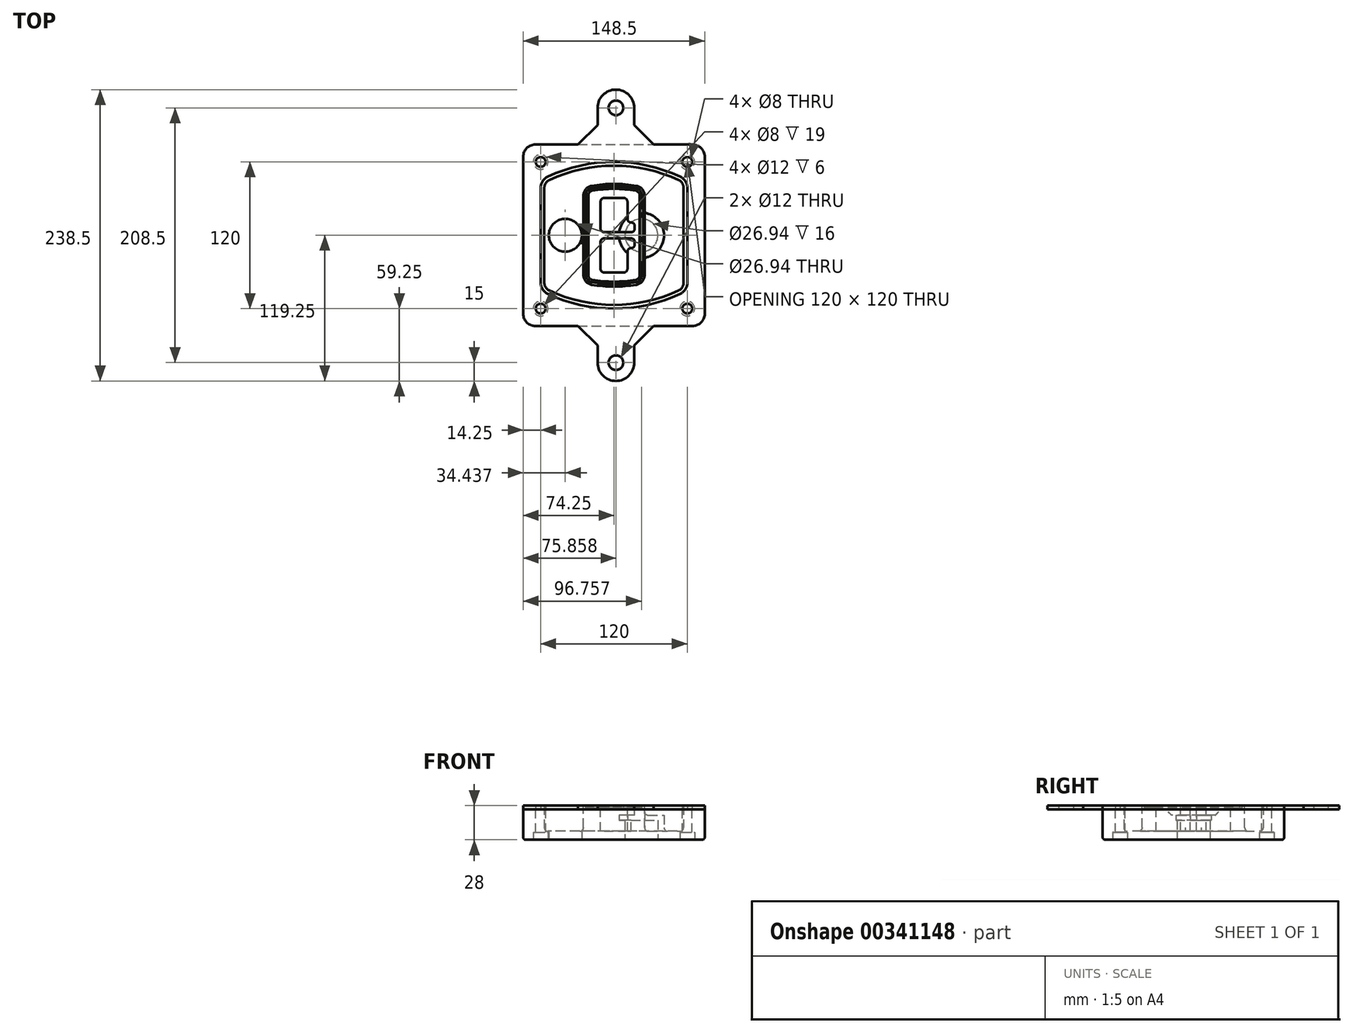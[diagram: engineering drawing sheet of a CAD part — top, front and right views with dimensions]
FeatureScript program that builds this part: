
annotation { "Feature Type Name" : "Feature", "Feature Type Description" : "" }
export const myFeature = defineFeature(function(context is Context, id is Id, definition is map)
    precondition{}
    {
        {
            var Q0;
            Q0=qCreatedBy(makeId("Top.planeOp"),FACE);
            var sketch = newSketch(context, id + "F0", { "sketchPlane" : qUnion([Q0])});
            skPoint(sketch, "E0.rect.middle", {"position": v(0, 0) * mm});
            skLineSegment(sketch, "E1.bottom", {"start": v(-64.25, -74.25) * mm, "end": v(64.25, -74.25) * mm});
            skLineSegment(sketch, "E1.top", {"start": v(-64.25, 74.25) * mm, "end": v(64.25, 74.25) * mm});
            skLineSegment(sketch, "E1.left", {"start": v(-74.25, -64.25) * mm, "end": v(-74.25, 64.25) * mm});
            skLineSegment(sketch, "E1.right", {"start": v(74.25, -64.25) * mm, "end": v(74.25, 64.25) * mm});
            skLineSegment(sketch, "E2", {"start": v(-74.25, 74.25) * mm, "end": v(74.25, -74.25) * mm, "construction": true});
            skLineSegment(sketch, "E3", {"start": v(74.25, 74.25) * mm, "end": v(-74.25, -74.25) * mm, "construction": true});
            skCircle(sketch, "E4", {"center": v(-60, 60) * mm, "radius": 4 * mm});
            skCircle(sketch, "E5", {"center": v(60, 60) * mm, "radius": 4 * mm});
            skCircle(sketch, "E6", {"center": v(60, -60) * mm, "radius": 4 * mm});
            skCircle(sketch, "E7", {"center": v(-60, -60) * mm, "radius": 4 * mm});
            skLineSegment(sketch, "E8", {"start": v(-60, 60) * mm, "end": v(60, 60) * mm, "construction": true});
            skLineSegment(sketch, "E9", {"start": v(60, 60) * mm, "end": v(60, -60) * mm, "construction": true});
            skLineSegment(sketch, "E10", {"start": v(60, -60) * mm, "end": v(-60, -60) * mm, "construction": true});
            skLineSegment(sketch, "E11", {"start": v(-60, -60) * mm, "end": v(-60, 60) * mm, "construction": true});
            skLineSegment(sketch, "E12", {"start": v(-60, 38.83) * mm, "end": v(-60, -38.83) * mm});
            skLineSegment(sketch, "E13", {"start": v(60, 38.83) * mm, "end": v(60, -38.83) * mm});
            skArc(sketch, "E14", {"start": v(54.26, 47.88) * mm, "mid": v(0, 60) * mm, "end": v(-54.26, 47.88) * mm});
            skArc(sketch, "E15", {"start": v(-54.26, -47.88) * mm, "mid": v(0, -60) * mm, "end": v(54.26, -47.88) * mm});
            skLineSegment(sketch, "E16", {"start": v(-60, 0) * mm, "end": v(60, 0) * mm, "construction": true});
            skPoint(sketch, "E17.visualSharp", {"position": v(-60, -45) * mm});
            skArc(sketch, "E17.filletArc", {"start": v(-60, -38.83) * mm, "mid": v(-58.44, -44.2) * mm, "end": v(-54.26, -47.88) * mm});
            skPoint(sketch, "E18.visualSharp", {"position": v(-60, 45) * mm});
            skArc(sketch, "E18.filletArc", {"start": v(-54.26, 47.88) * mm, "mid": v(-58.44, 44.2) * mm, "end": v(-60, 38.83) * mm});
            skPoint(sketch, "E19.visualSharp", {"position": v(60, 45) * mm});
            skArc(sketch, "E19.filletArc", {"start": v(60, 38.83) * mm, "mid": v(58.44, 44.2) * mm, "end": v(54.26, 47.88) * mm});
            skPoint(sketch, "E20.visualSharp", {"position": v(60, -45) * mm});
            skArc(sketch, "E20.filletArc", {"start": v(54.26, -47.88) * mm, "mid": v(58.44, -44.2) * mm, "end": v(60, -38.83) * mm});
            skPoint(sketch, "E21.visualSharp", {"position": v(-74.25, 74.25) * mm});
            skArc(sketch, "E21.filletArc", {"start": v(-64.25, 74.25) * mm, "mid": v(-71.32, 71.32) * mm, "end": v(-74.25, 64.25) * mm});
            skPoint(sketch, "E22.visualSharp", {"position": v(74.25, 74.25) * mm});
            skArc(sketch, "E22.filletArc", {"start": v(74.25, 64.25) * mm, "mid": v(71.32, 71.32) * mm, "end": v(64.25, 74.25) * mm});
            skPoint(sketch, "E23.visualSharp", {"position": v(74.25, -74.25) * mm});
            skArc(sketch, "E23.filletArc", {"start": v(64.25, -74.25) * mm, "mid": v(71.32, -71.32) * mm, "end": v(74.25, -64.25) * mm});
            skPoint(sketch, "E24.visualSharp", {"position": v(-74.25, -74.25) * mm});
            skArc(sketch, "E24.filletArc", {"start": v(-74.25, -64.25) * mm, "mid": v(-71.32, -71.32) * mm, "end": v(-64.25, -74.25) * mm});
            skArc(sketch, "E25.0", {"start": v(57, 38.83) * mm, "mid": v(55.9, 42.58) * mm, "end": v(52.98, 45.17) * mm});
            skLineSegment(sketch, "E25.1", {"start": v(57, 38.83) * mm, "end": v(57, -38.83) * mm});
            skArc(sketch, "E25.2", {"start": v(52.98, -45.17) * mm, "mid": v(55.9, -42.58) * mm, "end": v(57, -38.83) * mm});
            skArc(sketch, "E25.3", {"start": v(-52.98, -45.17) * mm, "mid": v(0, -57) * mm, "end": v(52.98, -45.17) * mm});
            skArc(sketch, "E25.4", {"start": v(-57, -38.83) * mm, "mid": v(-55.9, -42.58) * mm, "end": v(-52.98, -45.17) * mm});
            skArc(sketch, "E25.5", {"start": v(52.98, 45.17) * mm, "mid": v(0, 57) * mm, "end": v(-52.98, 45.17) * mm});
            skLineSegment(sketch, "E25.6", {"start": v(-57, 38.83) * mm, "end": v(-57, -38.83) * mm});
            skArc(sketch, "E25.7", {"start": v(-52.98, 45.17) * mm, "mid": v(-55.9, 42.58) * mm, "end": v(-57, 38.83) * mm});
            skArc(sketch, "E26.0", {"start": v(-55.96, 51.5) * mm, "mid": v(-61.82, 46.33) * mm, "end": v(-64, 38.83) * mm});
            skArc(sketch, "E26.1", {"start": v(55.96, 51.5) * mm, "mid": v(0, 64) * mm, "end": v(-55.96, 51.5) * mm});
            skArc(sketch, "E26.2", {"start": v(64, 38.83) * mm, "mid": v(61.82, 46.33) * mm, "end": v(55.96, 51.5) * mm});
            skLineSegment(sketch, "E26.3", {"start": v(64, 38.83) * mm, "end": v(64, -38.83) * mm});
            skArc(sketch, "E26.4", {"start": v(55.96, -51.5) * mm, "mid": v(61.82, -46.33) * mm, "end": v(64, -38.83) * mm});
            skLineSegment(sketch, "E26.5", {"start": v(-64, 38.83) * mm, "end": v(-64, -38.83) * mm});
            skArc(sketch, "E26.6", {"start": v(-55.96, -51.5) * mm, "mid": v(0, -64) * mm, "end": v(55.96, -51.5) * mm});
            skArc(sketch, "E26.7", {"start": v(-64, -38.83) * mm, "mid": v(-61.82, -46.33) * mm, "end": v(-55.96, -51.5) * mm});
            skSolve(sketch);
        }
        {
            var Q0;
            Q0=makeQuery(id+"F0.imprint","IMPRINT",FACE,{"disambiguationData":[TD([[makeQuery(id+"F0.imprint","IMPRINT",EDGE,{"derivedFrom":sQuery(id+"F0.wireOp",EDGE,"E1.bottom")}),1.0]])]});
            var Q1;
            Q1=makeQuery(id+"F0.imprint","IMPRINT",FACE,{"disambiguationData":[TD([[makeQuery(id+"F0.imprint","IMPRINT",EDGE,{"derivedFrom":sQuery(id+"F0.wireOp",EDGE,"E12")}),1.0]])]});
            var Q2;
            Q2=makeQuery(id+"F0.imprint","IMPRINT",FACE,{"disambiguationData":[TD([[makeQuery(id+"F0.imprint","IMPRINT",EDGE,{"derivedFrom":sQuery(id+"F0.wireOp",EDGE,"E25.0")}),1.0]])]});
            var Q3;
            Q3=makeQuery(id+"F0.imprint","IMPRINT",FACE,{"disambiguationData":[TD([[makeQuery(id+"F0.imprint","IMPRINT",EDGE,{"derivedFrom":sQuery(id+"F0.wireOp",EDGE,"E12")}),-1.0]])]});
            extrude(context, id + "F1", {"entities" : qUnion([Q0, Q1, Q2, Q3]), "oppositeDirection" : true, "depth" : 25 * mm});
        }
        {
            var Q0;
            Q0=makeQuery(id+"F0.imprint","IMPRINT",FACE,{"disambiguationData":[TD([[makeQuery(id+"F0.imprint","IMPRINT",EDGE,{"derivedFrom":sQuery(id+"F0.wireOp",EDGE,"E12")}),1.0]])]});
            extrude(context, id + "F2", {"entities" : qUnion([Q0]), "operationType" : NewBodyOperationType.ADD, "depth" : 3 * mm});
        }
        {
            var Q0;
            Q0=makeQuery(id+"F0.imprint","IMPRINT",FACE,{"disambiguationData":[TD([[makeQuery(id+"F0.imprint","IMPRINT",EDGE,{"derivedFrom":sQuery(id+"F0.wireOp",EDGE,"E25.0")}),1.0]])]});
            extrude(context, id + "F3", {"entities" : qUnion([Q0]), "operationType" : NewBodyOperationType.REMOVE, "oppositeDirection" : true, "depth" : 18 * mm});
        }
        {
            var Q0;
            Q0=makeQuery(id+"F2.opExtrude","CAP_FACE",FACE,{"disambiguationData":[OSD([sQuery(id+"F0.wireOp",EDGE,"E12"),sQuery(id+"F0.wireOp",EDGE,"E13"),sQuery(id+"F0.wireOp",EDGE,"E14"),sQuery(id+"F0.wireOp",EDGE,"E15"),sQuery(id+"F0.wireOp",EDGE,"E17.filletArc"),sQuery(id+"F0.wireOp",EDGE,"E18.filletArc"),sQuery(id+"F0.wireOp",EDGE,"E19.filletArc"),sQuery(id+"F0.wireOp",EDGE,"E20.filletArc"),sQuery(id+"F0.wireOp",EDGE,"E25.0"),sQuery(id+"F0.wireOp",EDGE,"E25.1"),sQuery(id+"F0.wireOp",EDGE,"E25.2"),sQuery(id+"F0.wireOp",EDGE,"E25.3"),sQuery(id+"F0.wireOp",EDGE,"E25.4"),sQuery(id+"F0.wireOp",EDGE,"E25.5"),sQuery(id+"F0.wireOp",EDGE,"E25.6"),sQuery(id+"F0.wireOp",EDGE,"E25.7")])],"isStart":false});
            var sketch = newSketch(context, id + "F4", { "sketchPlane" : qUnion([Q0])});
            skArc(sketch, "E27.0", {"start": v(-18.34, -40.45) * mm, "mid": v(0, -42) * mm, "end": v(18.34, -40.45) * mm});
            skArc(sketch, "E28.0", {"start": v(18.34, 40.45) * mm, "mid": v(0, 42) * mm, "end": v(-18.34, 40.45) * mm});
            skLineSegment(sketch, "E29", {"start": v(-25, 32.57) * mm, "end": v(-25, -32.57) * mm});
            skLineSegment(sketch, "E30", {"start": v(25, 32.57) * mm, "end": v(25, -32.57) * mm});
            skLineSegment(sketch, "E31", {"start": v(-25, 39.1) * mm, "end": v(25, 39.1) * mm, "construction": true});
            skLineSegment(sketch, "E32", {"start": v(-25, -39.1) * mm, "end": v(25, -39.1) * mm, "construction": true});
            skPoint(sketch, "E33.visualSharp", {"position": v(-25, 39.1) * mm});
            skArc(sketch, "E33.filletArc", {"start": v(-18.34, 40.45) * mm, "mid": v(-23.11, 37.73) * mm, "end": v(-25, 32.57) * mm});
            skPoint(sketch, "E34.visualSharp", {"position": v(25, 39.1) * mm});
            skArc(sketch, "E34.filletArc", {"start": v(25, 32.57) * mm, "mid": v(23.11, 37.73) * mm, "end": v(18.34, 40.45) * mm});
            skPoint(sketch, "E35.visualSharp", {"position": v(25, -39.1) * mm});
            skArc(sketch, "E35.filletArc", {"start": v(18.34, -40.45) * mm, "mid": v(23.11, -37.73) * mm, "end": v(25, -32.57) * mm});
            skPoint(sketch, "E36.visualSharp", {"position": v(-25, -39.1) * mm});
            skArc(sketch, "E36.filletArc", {"start": v(-25, -32.57) * mm, "mid": v(-23.11, -37.73) * mm, "end": v(-18.34, -40.45) * mm});
            skArc(sketch, "E37.0", {"start": v(52.98, 45.17) * mm, "mid": v(0, 57) * mm, "end": v(-52.98, 45.17) * mm});
            skArc(sketch, "E37.1", {"start": v(-52.98, 45.17) * mm, "mid": v(-55.9, 42.58) * mm, "end": v(-57, 38.83) * mm});
            skLineSegment(sketch, "E37.2", {"start": v(-57, 38.83) * mm, "end": v(-57, -38.83) * mm});
            skArc(sketch, "E37.3", {"start": v(-57, -38.83) * mm, "mid": v(-55.9, -42.58) * mm, "end": v(-52.98, -45.17) * mm});
            skArc(sketch, "E37.4", {"start": v(-52.98, -45.17) * mm, "mid": v(0, -57) * mm, "end": v(52.98, -45.17) * mm});
            skArc(sketch, "E37.5", {"start": v(52.98, -45.17) * mm, "mid": v(55.9, -42.58) * mm, "end": v(57, -38.83) * mm});
            skLineSegment(sketch, "E37.6", {"start": v(57, 38.83) * mm, "end": v(57, -38.83) * mm});
            skArc(sketch, "E37.7", {"start": v(57, 38.83) * mm, "mid": v(55.9, 42.58) * mm, "end": v(52.98, 45.17) * mm});
            skLineSegment(sketch, "E38.0", {"start": v(23, 32.57) * mm, "end": v(23, -32.57) * mm});
            skArc(sketch, "E38.1", {"start": v(18, -38.48) * mm, "mid": v(21.58, -36.44) * mm, "end": v(23, -32.57) * mm});
            skArc(sketch, "E38.2", {"start": v(-18, -38.48) * mm, "mid": v(0, -40) * mm, "end": v(18, -38.48) * mm});
            skArc(sketch, "E38.3", {"start": v(-23, -32.57) * mm, "mid": v(-21.58, -36.44) * mm, "end": v(-18, -38.48) * mm});
            skLineSegment(sketch, "E38.4", {"start": v(-23, 32.57) * mm, "end": v(-23, -32.57) * mm});
            skArc(sketch, "E38.5", {"start": v(23, 32.57) * mm, "mid": v(21.58, 36.44) * mm, "end": v(18, 38.48) * mm});
            skArc(sketch, "E38.6", {"start": v(-18, 38.48) * mm, "mid": v(-21.58, 36.44) * mm, "end": v(-23, 32.57) * mm});
            skArc(sketch, "E38.7", {"start": v(18, 38.48) * mm, "mid": v(0, 40) * mm, "end": v(-18, 38.48) * mm});
            skArc(sketch, "E39.0", {"start": v(21, 32.57) * mm, "mid": v(20.06, 35.15) * mm, "end": v(17.67, 36.5) * mm});
            skLineSegment(sketch, "E39.1", {"start": v(21, 32.57) * mm, "end": v(21, -32.57) * mm});
            skArc(sketch, "E39.2", {"start": v(17.67, -36.5) * mm, "mid": v(20.06, -35.15) * mm, "end": v(21, -32.57) * mm});
            skArc(sketch, "E39.3", {"start": v(-17.67, -36.5) * mm, "mid": v(0, -38) * mm, "end": v(17.67, -36.5) * mm});
            skArc(sketch, "E39.4", {"start": v(-21, -32.57) * mm, "mid": v(-20.06, -35.15) * mm, "end": v(-17.67, -36.5) * mm});
            skArc(sketch, "E39.5", {"start": v(17.67, 36.5) * mm, "mid": v(0, 38) * mm, "end": v(-17.67, 36.5) * mm});
            skLineSegment(sketch, "E39.6", {"start": v(-21, 32.57) * mm, "end": v(-21, -32.57) * mm});
            skArc(sketch, "E39.7", {"start": v(-17.67, 36.5) * mm, "mid": v(-20.06, 35.15) * mm, "end": v(-21, 32.57) * mm});
            skLineSegment(sketch, "E40", {"start": v(-25, 0) * mm, "end": v(25, 0) * mm, "construction": true});
            skLineSegment(sketch, "E41", {"start": v(-11, 5.5) * mm, "end": v(-11, 27.5) * mm});
            skLineSegment(sketch, "E42", {"start": v(-8, 30.5) * mm, "end": v(8, 30.5) * mm});
            skLineSegment(sketch, "E43", {"start": v(11, 27.5) * mm, "end": v(11, 13.5) * mm});
            skLineSegment(sketch, "E44", {"start": v(14, 10.5) * mm, "end": v(14, 10.5) * mm});
            skLineSegment(sketch, "E45", {"start": v(17, 7.5) * mm, "end": v(17, 5.5) * mm});
            skLineSegment(sketch, "E46", {"start": v(14, 2.5) * mm, "end": v(-8, 2.5) * mm});
            skPoint(sketch, "E47.visualSharp", {"position": v(-11, 30.5) * mm});
            skArc(sketch, "E47.filletArc", {"start": v(-8, 30.5) * mm, "mid": v(-10.12, 29.62) * mm, "end": v(-11, 27.5) * mm});
            skPoint(sketch, "E48.visualSharp", {"position": v(11, 30.5) * mm});
            skArc(sketch, "E48.filletArc", {"start": v(11, 27.5) * mm, "mid": v(10.12, 29.62) * mm, "end": v(8, 30.5) * mm});
            skPoint(sketch, "E49.visualSharp", {"position": v(11, 10.5) * mm});
            skArc(sketch, "E49.filletArc", {"start": v(11, 13.5) * mm, "mid": v(11.88, 11.38) * mm, "end": v(14, 10.5) * mm});
            skPoint(sketch, "E50.visualSharp", {"position": v(17, 10.5) * mm});
            skArc(sketch, "E50.filletArc", {"start": v(17, 7.5) * mm, "mid": v(16.12, 9.62) * mm, "end": v(14, 10.5) * mm});
            skPoint(sketch, "E51.visualSharp", {"position": v(17, 2.5) * mm});
            skArc(sketch, "E51.filletArc", {"start": v(14, 2.5) * mm, "mid": v(16.12, 3.38) * mm, "end": v(17, 5.5) * mm});
            skPoint(sketch, "E52.visualSharp", {"position": v(-11, 2.5) * mm});
            skArc(sketch, "E52.filletArc", {"start": v(-11, 5.5) * mm, "mid": v(-10.12, 3.38) * mm, "end": v(-8, 2.5) * mm});
            skLineSegment(sketch, "E53.0.MirrorCS", {"start": v(14, -2.5) * mm, "end": v(-8, -2.5) * mm});
            skArc(sketch, "E54.0.MirrorCS", {"start": v(-11, -5.5) * mm, "mid": v(-10.12, -3.38) * mm, "end": v(-8, -2.5) * mm});
            skLineSegment(sketch, "E55.0.MirrorCS", {"start": v(-11, -5.5) * mm, "end": v(-11, -27.5) * mm});
            skArc(sketch, "E56.0.MirrorCS", {"start": v(-8, -30.5) * mm, "mid": v(-10.12, -29.62) * mm, "end": v(-11, -27.5) * mm});
            skLineSegment(sketch, "E57.0.MirrorCS", {"start": v(-8, -30.5) * mm, "end": v(8, -30.5) * mm});
            skArc(sketch, "E58.0.MirrorCS", {"start": v(11, -27.5) * mm, "mid": v(10.12, -29.62) * mm, "end": v(8, -30.5) * mm});
            skLineSegment(sketch, "E59.0.MirrorCS", {"start": v(11, -27.5) * mm, "end": v(11, -13.5) * mm});
            skArc(sketch, "E60.0.MirrorCS", {"start": v(11, -13.5) * mm, "mid": v(11.88, -11.38) * mm, "end": v(14, -10.5) * mm});
            skArc(sketch, "E61.0.MirrorCS", {"start": v(17, -7.5) * mm, "mid": v(16.12, -9.62) * mm, "end": v(14, -10.5) * mm});
            skLineSegment(sketch, "E62.0.MirrorCS", {"start": v(17, -7.5) * mm, "end": v(17, -5.5) * mm});
            skArc(sketch, "E63.0.MirrorCS", {"start": v(14, -2.5) * mm, "mid": v(16.12, -3.38) * mm, "end": v(17, -5.5) * mm});
            skSolve(sketch);
        }
        {
            var Q0;
            Q0=makeQuery(id+"F4.imprint","IMPRINT",FACE,{"disambiguationData":[TD([[makeQuery(id+"F4.imprint","IMPRINT",EDGE,{"derivedFrom":sQuery(id+"F4.wireOp",EDGE,"E27.0")}),1.0]])]});
            var Q1;
            Q1=makeQuery(id+"F4.imprint","IMPRINT",FACE,{"disambiguationData":[TD([[makeQuery(id+"F4.imprint","IMPRINT",EDGE,{"derivedFrom":sQuery(id+"F4.wireOp",EDGE,"E38.0")}),-1.0]])]});
            var Q2;
            Q2=makeQuery(id+"F4.imprint","IMPRINT",FACE,{"disambiguationData":[TD([[makeQuery(id+"F4.imprint","IMPRINT",EDGE,{"derivedFrom":sQuery(id+"F4.wireOp",EDGE,"E39.0")}),1.0]])]});
            extrude(context, id + "F5", {"entities" : qUnion([Q0, Q1, Q2]), "operationType" : NewBodyOperationType.ADD, "endBound" : BoundingType.UP_TO_NEXT, "oppositeDirection" : true, "depth" : 25 * mm});
        }
        {
            var Q0;
            Q0=makeQuery(id+"F4.imprint","IMPRINT",FACE,{"disambiguationData":[TD([[makeQuery(id+"F4.imprint","IMPRINT",EDGE,{"derivedFrom":sQuery(id+"F4.wireOp",EDGE,"E38.0")}),-1.0]])]});
            extrude(context, id + "F6", {"entities" : qUnion([Q0]), "operationType" : NewBodyOperationType.REMOVE, "oppositeDirection" : true, "depth" : 2 * mm});
        }
        {
            var Q0;
            Q0=makeQuery(id+"F1.opExtrude","CAP_FACE",FACE,{"disambiguationData":[OSD([sQuery(id+"F0.wireOp",EDGE,"E1.bottom"),sQuery(id+"F0.wireOp",EDGE,"E1.top"),sQuery(id+"F0.wireOp",EDGE,"E1.left"),sQuery(id+"F0.wireOp",EDGE,"E1.right"),sQuery(id+"F0.wireOp",EDGE,"E4"),sQuery(id+"F0.wireOp",EDGE,"E5"),sQuery(id+"F0.wireOp",EDGE,"E6"),sQuery(id+"F0.wireOp",EDGE,"E7"),sQuery(id+"F0.wireOp",EDGE,"E21.filletArc"),sQuery(id+"F0.wireOp",EDGE,"E22.filletArc"),sQuery(id+"F0.wireOp",EDGE,"E23.filletArc"),sQuery(id+"F0.wireOp",EDGE,"E24.filletArc")])],"isStart":false});
            var sketch = newSketch(context, id + "F7", { "sketchPlane" : qUnion([Q0])});
            skCircle(sketch, "E64", {"center": v(22.5, 0) * mm, "radius": 13.47 * mm});
            skCircle(sketch, "E65", {"center": v(-39.81, 0) * mm, "radius": 13.47 * mm});
            skLineSegment(sketch, "E66", {"start": v(74.25, 0) * mm, "end": v(-74.25, 0) * mm});
            skCircle(sketch, "E67", {"center": v(22.5, 0) * mm, "radius": 18.47 * mm});
            skCircle(sketch, "E68", {"center": v(60, -60) * mm, "radius": 6 * mm});
            skCircle(sketch, "E69", {"center": v(-60, -60) * mm, "radius": 6 * mm});
            skCircle(sketch, "E70", {"center": v(-60, 60) * mm, "radius": 6 * mm});
            skCircle(sketch, "E71", {"center": v(60, 60) * mm, "radius": 6 * mm});
            skSolve(sketch);
        }
        {
            var Q0;
            {var subQ1=sQuery(id+"F7.wireOp",EDGE,"E66");var subQ4=sQuery(id+"F7.wireOp",EDGE,"E64");var subQ6=makeQuery(id+"F7.imprint","INTERSECT",VERTEX,{"disambiguationData":[OD(0.0)],"derivedFrom":[subQ4,subQ1]});Q0=makeQuery(id+"F7.imprint","IMPRINT",FACE,{"disambiguationData":[TD([[makeQuery(id+"F7.imprint","IMPRINT",EDGE,{"disambiguationData":[TD([[subQ6,-1.0]])],"derivedFrom":subQ4}),-1.0]])]});}
            var Q1;
            {var subQ0=sQuery(id+"F7.wireOp",EDGE,"E66");var subQ1=sQuery(id+"F7.wireOp",EDGE,"E64");var subQ3=makeQuery(id+"F7.imprint","INTERSECT",VERTEX,{"disambiguationData":[OD(0.0)],"derivedFrom":[subQ1,subQ0]});Q1=makeQuery(id+"F7.imprint","IMPRINT",FACE,{"disambiguationData":[TD([[makeQuery(id+"F7.imprint","IMPRINT",EDGE,{"disambiguationData":[TD([[subQ3,-1.0]])],"derivedFrom":subQ1}),1.0]])]});}
            var Q2;
            {var subQ0=sQuery(id+"F7.wireOp",EDGE,"E66");var subQ1=sQuery(id+"F7.wireOp",EDGE,"E64");var subQ3=makeQuery(id+"F7.imprint","INTERSECT",VERTEX,{"disambiguationData":[OD(0.0)],"derivedFrom":[subQ1,subQ0]});Q2=makeQuery(id+"F7.imprint","IMPRINT",FACE,{"disambiguationData":[TD([[makeQuery(id+"F7.imprint","IMPRINT",EDGE,{"disambiguationData":[TD([[subQ3,1.0]])],"derivedFrom":subQ1}),1.0]])]});}
            var Q3;
            {var subQ1=sQuery(id+"F7.wireOp",EDGE,"E66");var subQ4=sQuery(id+"F7.wireOp",EDGE,"E64");var subQ6=makeQuery(id+"F7.imprint","INTERSECT",VERTEX,{"disambiguationData":[OD(0.0)],"derivedFrom":[subQ4,subQ1]});Q3=makeQuery(id+"F7.imprint","IMPRINT",FACE,{"disambiguationData":[TD([[makeQuery(id+"F7.imprint","IMPRINT",EDGE,{"disambiguationData":[TD([[subQ6,1.0]])],"derivedFrom":subQ4}),-1.0]])]});}
            extrude(context, id + "F8", {"entities" : qUnion([Q0, Q1, Q2, Q3]), "operationType" : NewBodyOperationType.ADD, "oppositeDirection" : true, "depth" : 20 * mm});
        }
        {
            var Q0;
            {var subQ0=sQuery(id+"F7.wireOp",EDGE,"E66");var subQ1=sQuery(id+"F7.wireOp",EDGE,"E64");var subQ3=makeQuery(id+"F7.imprint","INTERSECT",VERTEX,{"disambiguationData":[OD(0.0)],"derivedFrom":[subQ1,subQ0]});Q0=makeQuery(id+"F7.imprint","IMPRINT",FACE,{"disambiguationData":[TD([[makeQuery(id+"F7.imprint","IMPRINT",EDGE,{"disambiguationData":[TD([[subQ3,-1.0]])],"derivedFrom":subQ1}),1.0]])]});}
            var Q1;
            {var subQ0=sQuery(id+"F7.wireOp",EDGE,"E66");var subQ1=sQuery(id+"F7.wireOp",EDGE,"E64");var subQ3=makeQuery(id+"F7.imprint","INTERSECT",VERTEX,{"disambiguationData":[OD(0.0)],"derivedFrom":[subQ1,subQ0]});Q1=makeQuery(id+"F7.imprint","IMPRINT",FACE,{"disambiguationData":[TD([[makeQuery(id+"F7.imprint","IMPRINT",EDGE,{"disambiguationData":[TD([[subQ3,1.0]])],"derivedFrom":subQ1}),1.0]])]});}
            extrude(context, id + "F9", {"entities" : qUnion([Q0, Q1]), "operationType" : NewBodyOperationType.REMOVE, "oppositeDirection" : true, "depth" : 16 * mm});
        }
        {
            var Q0;
            {var subQ0=sQuery(id+"F7.wireOp",EDGE,"E66");var subQ1=sQuery(id+"F7.wireOp",EDGE,"E65");var subQ3=makeQuery(id+"F7.imprint","INTERSECT",VERTEX,{"disambiguationData":[OD(0.0)],"derivedFrom":[subQ1,subQ0]});Q0=makeQuery(id+"F7.imprint","IMPRINT",FACE,{"disambiguationData":[TD([[makeQuery(id+"F7.imprint","IMPRINT",EDGE,{"disambiguationData":[TD([[subQ3,-1.0]])],"derivedFrom":subQ1}),1.0]])]});}
            var Q1;
            {var subQ0=sQuery(id+"F7.wireOp",EDGE,"E66");var subQ1=sQuery(id+"F7.wireOp",EDGE,"E65");var subQ3=makeQuery(id+"F7.imprint","INTERSECT",VERTEX,{"disambiguationData":[OD(0.0)],"derivedFrom":[subQ1,subQ0]});Q1=makeQuery(id+"F7.imprint","IMPRINT",FACE,{"disambiguationData":[TD([[makeQuery(id+"F7.imprint","IMPRINT",EDGE,{"disambiguationData":[TD([[subQ3,1.0]])],"derivedFrom":subQ1}),1.0]])]});}
            extrude(context, id + "F10", {"entities" : qUnion([Q0, Q1]), "operationType" : NewBodyOperationType.REMOVE, "oppositeDirection" : true, "depth" : 25 * mm});
        }
        {
            var Q0;
            Q0=makeQuery(id+"F7.imprint","IMPRINT",FACE,{"disambiguationData":[TD([[makeQuery(id+"F7.imprint","IMPRINT",EDGE,{"derivedFrom":sQuery(id+"F7.wireOp",EDGE,"E68")}),1.0]])]});
            var Q1;
            Q1=makeQuery(id+"F7.imprint","IMPRINT",FACE,{"disambiguationData":[TD([[makeQuery(id+"F7.imprint","IMPRINT",EDGE,{"derivedFrom":makeQuery(id+"F1.opExtrude","CAP_EDGE",EDGE,{"disambiguationData":[OSD([sQuery(id+"F0.wireOp",EDGE,"E5")])],"isStart":false})}),-1.0]])]});
            var Q2;
            Q2=makeQuery(id+"F7.imprint","IMPRINT",FACE,{"disambiguationData":[TD([[makeQuery(id+"F7.imprint","IMPRINT",EDGE,{"derivedFrom":sQuery(id+"F7.wireOp",EDGE,"E69")}),1.0]])]});
            var Q3;
            Q3=makeQuery(id+"F7.imprint","IMPRINT",FACE,{"disambiguationData":[TD([[makeQuery(id+"F7.imprint","IMPRINT",EDGE,{"derivedFrom":makeQuery(id+"F1.opExtrude","CAP_EDGE",EDGE,{"disambiguationData":[OSD([sQuery(id+"F0.wireOp",EDGE,"E4")])],"isStart":false})}),-1.0]])]});
            var Q4;
            Q4=makeQuery(id+"F7.imprint","IMPRINT",FACE,{"disambiguationData":[TD([[makeQuery(id+"F7.imprint","IMPRINT",EDGE,{"derivedFrom":sQuery(id+"F7.wireOp",EDGE,"E70")}),1.0]])]});
            var Q5;
            Q5=makeQuery(id+"F7.imprint","IMPRINT",FACE,{"disambiguationData":[TD([[makeQuery(id+"F7.imprint","IMPRINT",EDGE,{"derivedFrom":makeQuery(id+"F1.opExtrude","CAP_EDGE",EDGE,{"disambiguationData":[OSD([sQuery(id+"F0.wireOp",EDGE,"E7")])],"isStart":false})}),-1.0]])]});
            var Q6;
            Q6=makeQuery(id+"F7.imprint","IMPRINT",FACE,{"disambiguationData":[TD([[makeQuery(id+"F7.imprint","IMPRINT",EDGE,{"derivedFrom":sQuery(id+"F7.wireOp",EDGE,"E71")}),1.0]])]});
            var Q7;
            Q7=makeQuery(id+"F7.imprint","IMPRINT",FACE,{"disambiguationData":[TD([[makeQuery(id+"F7.imprint","IMPRINT",EDGE,{"derivedFrom":makeQuery(id+"F1.opExtrude","CAP_EDGE",EDGE,{"disambiguationData":[OSD([sQuery(id+"F0.wireOp",EDGE,"E6")])],"isStart":false})}),-1.0]])]});
            extrude(context, id + "F11", {"entities" : qUnion([Q0, Q1, Q2, Q3, Q4, Q5, Q6, Q7]), "operationType" : NewBodyOperationType.REMOVE, "oppositeDirection" : true, "depth" : 6 * mm});
        }
        {
            var Q0;
            Q0=makeQuery(id+"F9.boolean.opBoolean","COPY",FACE,{"derivedFrom":makeQuery(id+"F9.opExtrude","CAP_FACE",FACE,{"disambiguationData":[OSD([sQuery(id+"F7.wireOp",EDGE,"E64")])],"isStart":false})});
            var sketch = newSketch(context, id + "F12", { "sketchPlane" : qUnion([Q0])});
            skArc(sketch, "E72.0", {"start": v(11, 14.45) * mm, "mid": v(6.45, 9.13) * mm, "end": v(4.2, 2.5) * mm});
            skArc(sketch, "E72.1", {"start": v(4.2, -2.5) * mm, "mid": v(6.45, -9.13) * mm, "end": v(11, -14.45) * mm});
            skLineSegment(sketch, "E73", {"start": v(4.2, -2.5) * mm, "end": v(14, -2.5) * mm});
            skLineSegment(sketch, "E74.0", {"start": v(14, 2.5) * mm, "end": v(4.2, 2.5) * mm});
            skArc(sketch, "E74.1", {"start": v(14, 2.5) * mm, "mid": v(16.12, 3.38) * mm, "end": v(17, 5.5) * mm});
            skLineSegment(sketch, "E74.2", {"start": v(17, 7.5) * mm, "end": v(17, 5.5) * mm});
            skArc(sketch, "E74.3", {"start": v(17, 7.5) * mm, "mid": v(16.12, 9.62) * mm, "end": v(14, 10.5) * mm});
            skArc(sketch, "E74.4", {"start": v(11, 13.5) * mm, "mid": v(11.88, 11.38) * mm, "end": v(14, 10.5) * mm});
            skLineSegment(sketch, "E74.5", {"start": v(11, 14.45) * mm, "end": v(11, 13.5) * mm});
            skLineSegment(sketch, "E74.7", {"start": v(14, -2.5) * mm, "end": v(4.2, -2.5) * mm});
            skArc(sketch, "E74.8", {"start": v(14, -2.5) * mm, "mid": v(16.12, -3.38) * mm, "end": v(17, -5.5) * mm});
            skLineSegment(sketch, "E74.9", {"start": v(17, -7.5) * mm, "end": v(17, -5.5) * mm});
            skArc(sketch, "E74.10", {"start": v(17, -7.5) * mm, "mid": v(16.12, -9.62) * mm, "end": v(14, -10.5) * mm});
            skArc(sketch, "E74.11", {"start": v(11, -13.5) * mm, "mid": v(11.88, -11.38) * mm, "end": v(14, -10.5) * mm});
            skLineSegment(sketch, "E74.12", {"start": v(11, -14.45) * mm, "end": v(11, -13.5) * mm});
            skPoint(sketch, "E75.orphan", {"position": v(11, -27.5) * mm});
            skPoint(sketch, "E76.orphan", {"position": v(-8, -2.5) * mm});
            skPoint(sketch, "E77.orphan", {"position": v(-8, 2.5) * mm});
            skPoint(sketch, "E78.orphan", {"position": v(11, 27.5) * mm});
            skSolve(sketch);
        }
        {
            var Q0;
            {var subQ7=sQuery(id+"F12.wireOp",EDGE,"E72.0");var subQ14=sQuery(id+"F12.wireOp",EDGE,"E72.1");var subQ16=sQuery(id+"F12.wireOp",EDGE,"E74.1");var subQ18=sQuery(id+"F12.wireOp",EDGE,"E74.8");Q0=qUnion([makeQuery(id+"F12.imprint","IMPRINT",FACE,{"disambiguationData":[TD([[makeQuery(id+"F12.imprint","IMPRINT",EDGE,{"derivedFrom":subQ7}),1.0]])]}),makeQuery(id+"F12.imprint","IMPRINT",FACE,{"disambiguationData":[TD([[makeQuery(id+"F12.imprint","IMPRINT",EDGE,{"derivedFrom":subQ14}),1.0]])]}),makeQuery(id+"F12.imprint","IMPRINT",FACE,{"disambiguationData":[TD([[makeQuery(id+"F12.imprint","IMPRINT",EDGE,{"derivedFrom":subQ16}),1.0]])]}),makeQuery(id+"F12.imprint","IMPRINT",FACE,{"disambiguationData":[TD([[makeQuery(id+"F12.imprint","IMPRINT",EDGE,{"derivedFrom":subQ18}),-1.0]])]})]);}
            var Q1;
            Q1=makeQuery(id+"F5.boolean.opBoolean","SPLIT",FACE,{"disambiguationData":[TD([makeQuery(id+"F5.opExtrude","SWEPT_FACE",FACE,{"disambiguationData":[OSD([sQuery(id+"F4.wireOp",EDGE,"E41")])]})])],"derivedFrom":makeQuery(id+"F3.boolean.opBoolean","COPY",FACE,{"derivedFrom":makeQuery(id+"F3.opExtrude","CAP_FACE",FACE,{"disambiguationData":[OSD([sQuery(id+"F0.wireOp",EDGE,"E25.0"),sQuery(id+"F0.wireOp",EDGE,"E25.1"),sQuery(id+"F0.wireOp",EDGE,"E25.2"),sQuery(id+"F0.wireOp",EDGE,"E25.3"),sQuery(id+"F0.wireOp",EDGE,"E25.4"),sQuery(id+"F0.wireOp",EDGE,"E25.5"),sQuery(id+"F0.wireOp",EDGE,"E25.6"),sQuery(id+"F0.wireOp",EDGE,"E25.7")])],"isStart":false})})});
            extrude(context, id + "F13", {"entities" : qUnion([Q0]), "operationType" : NewBodyOperationType.REMOVE, "endBound" : BoundingType.UP_TO_SURFACE, "endBoundEntityFace" : qUnion([Q1]), "depth" : 25 * mm});
        }
        {
            var Q0;
            Q0=makeQuery(id+"F3.boolean.opBoolean","COPY",EDGE,{"derivedFrom":makeQuery(id+"F3.opExtrude","CAP_EDGE",EDGE,{"disambiguationData":[OSD([sQuery(id+"F0.wireOp",EDGE,"E25.6")])],"isStart":false})});
            var Q1;
            Q1=makeQuery(id+"F8.boolean.opBoolean","INTERSECT",EDGE,{"derivedFrom":[makeQuery(id+"F5.opExtrude","SWEPT_FACE",FACE,{"disambiguationData":[OSD([sQuery(id+"F4.wireOp",EDGE,"E30")])]}),makeQuery(id+"F8.opExtrude","CAP_FACE",FACE,{"disambiguationData":[OSD([sQuery(id+"F7.wireOp",EDGE,"E67")])],"isStart":false})]});
            var Q2;
            Q2=makeQuery(id+"F8.boolean.opBoolean","INTERSECT",EDGE,{"disambiguationData":[OD(1.0)],"derivedFrom":[makeQuery(id+"F5.opExtrude","SWEPT_FACE",FACE,{"disambiguationData":[OSD([sQuery(id+"F4.wireOp",EDGE,"E30")])]}),makeQuery(id+"F8.opExtrude","SWEPT_FACE",FACE,{"disambiguationData":[OSD([sQuery(id+"F7.wireOp",EDGE,"E67")])]})]});
            var Q3;
            {var subQ0=sQuery(id+"F4.wireOp",EDGE,"E30");Q3=makeQuery(id+"F8.boolean.opBoolean","SPLIT",EDGE,{"disambiguationData":[TD([makeQuery(id+"F5.opExtrude","SWEPT_FACE",FACE,{"disambiguationData":[OSD([sQuery(id+"F4.wireOp",EDGE,"E35.filletArc")])]})])],"derivedFrom":makeQuery(id+"F5.opExtrude","CAP_EDGE",EDGE,{"disambiguationData":[OSD([subQ0])],"isStart":false})});}
            var Q4;
            {var subQ0=sQuery(id+"F0.wireOp",EDGE,"E25.7");var subQ1=sQuery(id+"F0.wireOp",EDGE,"E25.1");var subQ2=sQuery(id+"F0.wireOp",EDGE,"E25.6");var subQ3=sQuery(id+"F0.wireOp",EDGE,"E25.5");var subQ4=sQuery(id+"F0.wireOp",EDGE,"E25.4");var subQ5=sQuery(id+"F0.wireOp",EDGE,"E25.0");var subQ6=sQuery(id+"F0.wireOp",EDGE,"E25.2");var subQ7=sQuery(id+"F0.wireOp",EDGE,"E25.3");Q4=makeQuery(id+"F8.boolean.opBoolean","INTERSECT",EDGE,{"derivedFrom":[makeQuery(id+"F5.boolean.opBoolean","SPLIT",FACE,{"disambiguationData":[TD([makeQuery(id+"F2.opExtrude","SWEPT_FACE",FACE,{"disambiguationData":[OSD([subQ5])]})])],"derivedFrom":makeQuery(id+"F3.boolean.opBoolean","COPY",FACE,{"derivedFrom":makeQuery(id+"F3.opExtrude","CAP_FACE",FACE,{"disambiguationData":[OSD([subQ5,subQ1,subQ6,subQ7,subQ4,subQ3,subQ2,subQ0])],"isStart":false})})}),makeQuery(id+"F8.opExtrude","SWEPT_FACE",FACE,{"disambiguationData":[OSD([sQuery(id+"F7.wireOp",EDGE,"E67")])]})]});}
            var Q5;
            Q5=makeQuery(id+"F8.boolean.opBoolean","INTERSECT",EDGE,{"disambiguationData":[OD(0.0)],"derivedFrom":[makeQuery(id+"F5.opExtrude","SWEPT_FACE",FACE,{"disambiguationData":[OSD([sQuery(id+"F4.wireOp",EDGE,"E30")])]}),makeQuery(id+"F8.opExtrude","SWEPT_FACE",FACE,{"disambiguationData":[OSD([sQuery(id+"F7.wireOp",EDGE,"E67")])]})]});
            fillet(context, id + "F14", {"entities" : qUnion([Q0, Q1, Q2, Q3, Q4, Q5]), "radius" : 3 * mm, "tangentPropagation" : true, "allowEdgeOverflow" : false});
        }
        {
            var Q0;
            Q0=makeQuery(id+"F1.opExtrude","CAP_EDGE",EDGE,{"disambiguationData":[OSD([sQuery(id+"F0.wireOp",EDGE,"E1.bottom")])],"isStart":false});
            fillet(context, id + "F15", {"entities" : qUnion([Q0]), "radius" : 2 * mm, "tangentPropagation" : true, "allowEdgeOverflow" : false});
        }
        {
            var Q0;
            {var subQ0=sQuery(id+"F0.wireOp",EDGE,"E21.filletArc");var subQ1=sQuery(id+"F0.wireOp",EDGE,"E7");var subQ2=sQuery(id+"F0.wireOp",EDGE,"E6");var subQ3=sQuery(id+"F0.wireOp",EDGE,"E5");var subQ4=sQuery(id+"F0.wireOp",EDGE,"E4");var subQ5=sQuery(id+"F0.wireOp",EDGE,"E22.filletArc");var subQ6=sQuery(id+"F0.wireOp",EDGE,"E1.bottom");var subQ7=sQuery(id+"F0.wireOp",EDGE,"E1.right");var subQ8=sQuery(id+"F0.wireOp",EDGE,"E1.top");var subQ9=sQuery(id+"F0.wireOp",EDGE,"E1.left");var subQ10=sQuery(id+"F0.wireOp",EDGE,"E23.filletArc");var subQ11=sQuery(id+"F0.wireOp",EDGE,"E24.filletArc");Q0=makeQuery(id+"F2.boolean.opBoolean","SPLIT",FACE,{"disambiguationData":[TD([makeQuery(id+"F1.opExtrude","SWEPT_FACE",FACE,{"disambiguationData":[OSD([subQ6])]})])],"derivedFrom":makeQuery(id+"F1.opExtrude","CAP_FACE",FACE,{"disambiguationData":[OSD([subQ6,subQ8,subQ9,subQ7,subQ4,subQ3,subQ2,subQ1,subQ0,subQ5,subQ10,subQ11])],"isStart":true})});}
            var sketch = newSketch(context, id + "F16", { "sketchPlane" : qUnion([Q0])});
            skArc(sketch, "E79", {"start": v(16.6, 104.25) * mm, "mid": v(1.6, 119.25) * mm, "end": v(-13.4, 104.25) * mm});
            skLineSegment(sketch, "E80", {"start": v(16.6, 104.25) * mm, "end": v(16.6, 90.21) * mm});
            skCircle(sketch, "E81", {"center": v(1.6, 104.25) * mm, "radius": 6 * mm});
            skLineSegment(sketch, "E82", {"start": v(1.6, 104.25) * mm, "end": v(1.6, 74.25) * mm, "construction": true});
            skLineSegment(sketch, "E83", {"start": v(16.6, 90.21) * mm, "end": v(32.57, 74.25) * mm});
            skLineSegment(sketch, "E84.MirrorCS", {"start": v(-13.4, 104.25) * mm, "end": v(-13.4, 90.21) * mm});
            skArc(sketch, "E85.MirrorCS", {"start": v(-13.4, 104.25) * mm, "mid": v(1.6, 119.25) * mm, "end": v(16.6, 104.25) * mm});
            skLineSegment(sketch, "E86.MirrorCS", {"start": v(-13.4, 90.21) * mm, "end": v(-29.35, 74.25) * mm});
            skLineSegment(sketch, "E87", {"start": v(-74.25, 0) * mm, "end": v(74.25, 0) * mm, "construction": true});
            skLineSegment(sketch, "E88.MirrorCS", {"start": v(-13.4, -104.25) * mm, "end": v(-13.4, -90.21) * mm});
            skArc(sketch, "E89.MirrorCS", {"start": v(-13.4, -104.25) * mm, "mid": v(1.6, -119.25) * mm, "end": v(16.6, -104.25) * mm});
            skCircle(sketch, "E90.MirrorC", {"center": v(1.6, -104.25) * mm, "radius": 6 * mm});
            skLineSegment(sketch, "E91.MirrorCS", {"start": v(1.6, -104.25) * mm, "end": v(1.6, -74.25) * mm, "construction": true});
            skLineSegment(sketch, "E92.MirrorCS", {"start": v(16.6, -104.25) * mm, "end": v(16.6, -90.21) * mm});
            skLineSegment(sketch, "E93.MirrorCS", {"start": v(16.6, -90.21) * mm, "end": v(32.57, -74.25) * mm});
            skLineSegment(sketch, "E94.MirrorCS", {"start": v(-13.4, -90.21) * mm, "end": v(-29.35, -74.25) * mm});
            skSolve(sketch);
        }
        {
            var Q0;
            Q0=makeQuery(id+"F16.imprint","IMPRINT",FACE,{"disambiguationData":[TD([[makeQuery(id+"F16.imprint","IMPRINT",EDGE,{"derivedFrom":sQuery(id+"F16.wireOp",EDGE,"E88.MirrorCS")}),-1.0]])]});
            var Q1;
            {var subQ0=sQuery(id+"F16.wireOp",EDGE,"E83");Q1=makeQuery(id+"F16.imprint","IMPRINT",FACE,{"disambiguationData":[TD([[makeQuery(id+"F16.imprint","IMPRINT",EDGE,{"derivedFrom":subQ0}),-1.0]])]});}
            var Q2;
            Q2=makeQuery(id+"F16.imprint","IMPRINT",FACE,{"disambiguationData":[TD([[makeQuery(id+"F16.imprint","IMPRINT",EDGE,{"derivedFrom":makeQuery(id+"F1.opExtrude","CAP_EDGE",EDGE,{"disambiguationData":[OSD([sQuery(id+"F0.wireOp",EDGE,"E1.left")])],"isStart":true})}),-1.0]])]});
            var Q3;
            Q3=makeQuery(id+"F2.opExtrude","CAP_FACE",FACE,{"disambiguationData":[OSD([sQuery(id+"F0.wireOp",EDGE,"E12"),sQuery(id+"F0.wireOp",EDGE,"E13"),sQuery(id+"F0.wireOp",EDGE,"E14"),sQuery(id+"F0.wireOp",EDGE,"E15"),sQuery(id+"F0.wireOp",EDGE,"E17.filletArc"),sQuery(id+"F0.wireOp",EDGE,"E18.filletArc"),sQuery(id+"F0.wireOp",EDGE,"E19.filletArc"),sQuery(id+"F0.wireOp",EDGE,"E20.filletArc"),sQuery(id+"F0.wireOp",EDGE,"E25.0"),sQuery(id+"F0.wireOp",EDGE,"E25.1"),sQuery(id+"F0.wireOp",EDGE,"E25.2"),sQuery(id+"F0.wireOp",EDGE,"E25.3"),sQuery(id+"F0.wireOp",EDGE,"E25.4"),sQuery(id+"F0.wireOp",EDGE,"E25.5"),sQuery(id+"F0.wireOp",EDGE,"E25.6"),sQuery(id+"F0.wireOp",EDGE,"E25.7")])],"isStart":false});
            extrude(context, id + "F17", {"entities" : qUnion([Q0, Q1, Q2]), "endBound" : BoundingType.UP_TO_SURFACE, "endBoundEntityFace" : qUnion([Q3]), "depth" : 25 * mm});
        }
    });
